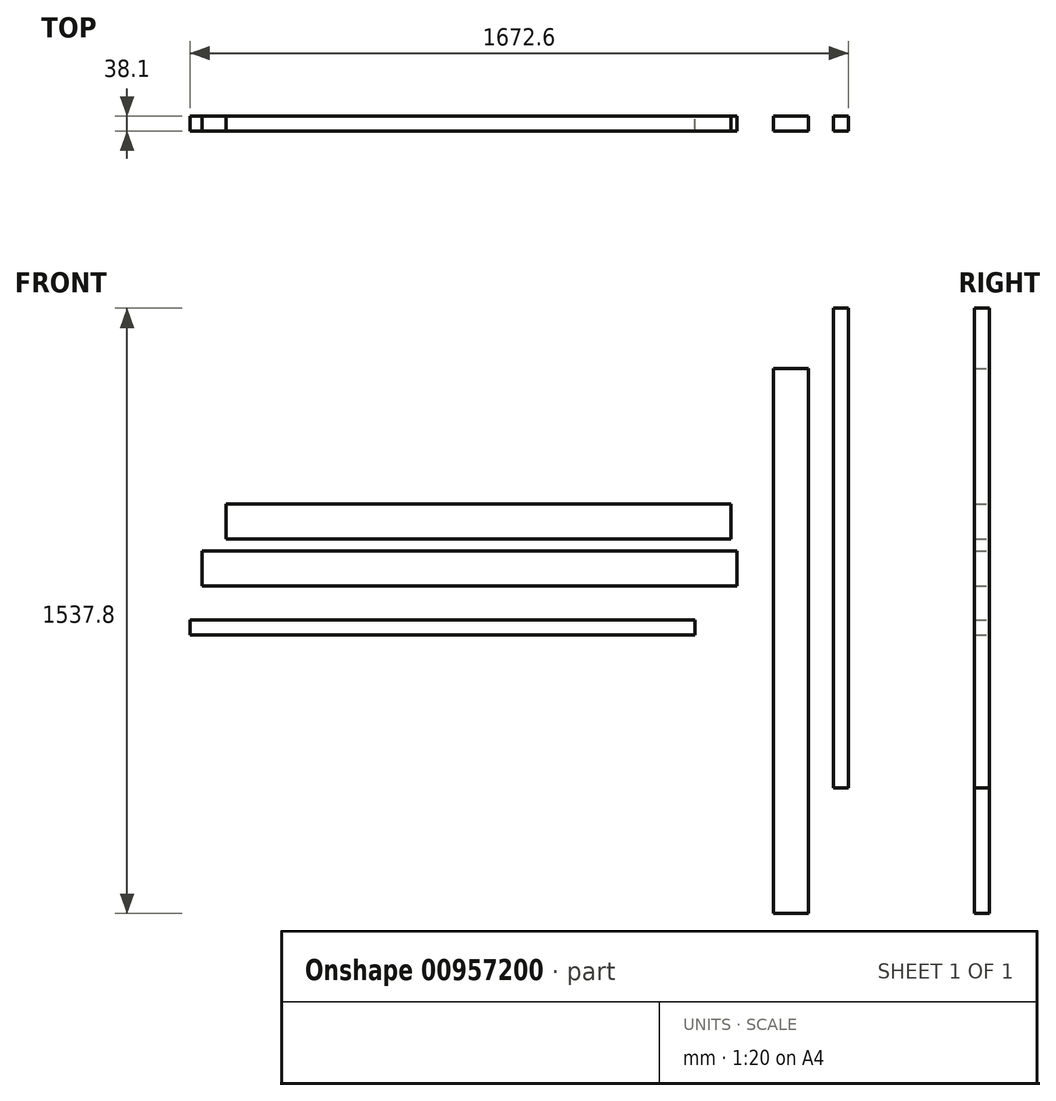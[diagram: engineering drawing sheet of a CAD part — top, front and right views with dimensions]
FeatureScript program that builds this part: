
annotation { "Feature Type Name" : "Feature", "Feature Type Description" : "" }
export const myFeature = defineFeature(function(context is Context, id is Id, definition is map)
    precondition{}
    {
        {
            var Q0;
            Q0=qCreatedBy(makeId("Front.planeOp"),FACE);
            var sketch = newSketch(context, id + "F0", { "sketchPlane" : qUnion([Q0])});
            skLineSegment(sketch, "E0.bottom", {"start": v(471.1, 163.2) * mm, "end": v(-811.6, 163.2) * mm});
            skLineSegment(sketch, "E0.top", {"start": v(471.1, 74.3) * mm, "end": v(-811.6, 74.3) * mm});
            skLineSegment(sketch, "E0.left", {"start": v(471.1, 163.2) * mm, "end": v(471.1, 74.3) * mm});
            skLineSegment(sketch, "E0.right", {"start": v(-811.6, 163.2) * mm, "end": v(-811.6, 74.3) * mm});
            skPoint(sketch, "E0.middle", {"position": v(-170.25, 118.74) * mm});
            skSolve(sketch);
        }
        {
            var Q0;
            Q0=qCreatedBy(makeId("Front.planeOp"),FACE);
            var sketch = newSketch(context, id + "F1", { "sketchPlane" : qUnion([Q0])});
            skLineSegment(sketch, "E1.bottom", {"start": v(487.25, -44.45) * mm, "end": v(-871.65, -44.45) * mm});
            skLineSegment(sketch, "E1.top", {"start": v(487.25, 44.45) * mm, "end": v(-871.65, 44.45) * mm});
            skLineSegment(sketch, "E1.left", {"start": v(487.25, -44.45) * mm, "end": v(487.25, 44.45) * mm});
            skLineSegment(sketch, "E1.right", {"start": v(-871.65, -44.45) * mm, "end": v(-871.65, 44.45) * mm});
            skPoint(sketch, "E1.middle", {"position": v(-192.2, 0) * mm});
            skSolve(sketch);
        }
        {
            var Q0;
            Q0=qCreatedBy(makeId("Front.planeOp"),FACE);
            var sketch = newSketch(context, id + "F2", { "sketchPlane" : qUnion([Q0])});
            skLineSegment(sketch, "E2.bottom", {"start": v(668.46, 507.39) * mm, "end": v(579.56, 507.39) * mm});
            skLineSegment(sketch, "E2.top", {"start": v(668.46, -876.91) * mm, "end": v(579.56, -876.91) * mm});
            skLineSegment(sketch, "E2.left", {"start": v(668.46, 507.39) * mm, "end": v(668.46, -876.91) * mm});
            skLineSegment(sketch, "E2.right", {"start": v(579.56, 507.39) * mm, "end": v(579.56, -876.91) * mm});
            skPoint(sketch, "E2.middle", {"position": v(624.01, -184.76) * mm});
            skSolve(sketch);
        }
        {
            var Q0;
            Q0=qSketchRegion(id+"F0",true);
            extrude(context, id + "F3", {"entities" : qUnion([Q0]), "depth" : 38.1 * mm, "offsetDistance" : 25.4 * mm});
        }
        {
            var Q0;
            Q0=makeQuery(id+"F1.imprint","IMPRINT",FACE,{"disambiguationData":[TD([[makeQuery(id+"F1.imprint","IMPRINT",EDGE,{"derivedFrom":sQuery(id+"F1.wireOp",EDGE,"E1.bottom")}),-1.0]])]});
            extrude(context, id + "F4", {"entities" : qUnion([Q0]), "depth" : 38.1 * mm, "offsetDistance" : 25.4 * mm});
        }
        {
            var Q0;
            Q0=makeQuery(id+"F2.imprint","IMPRINT",FACE,{"disambiguationData":[TD([[makeQuery(id+"F2.imprint","IMPRINT",EDGE,{"derivedFrom":sQuery(id+"F2.wireOp",EDGE,"E2.bottom")}),1.0]])]});
            extrude(context, id + "F5", {"entities" : qUnion([Q0]), "depth" : 38.1 * mm, "offsetDistance" : 25.4 * mm});
        }
        {
            var Q0;
            Q0=qCreatedBy(makeId("Front.planeOp"),FACE);
            var sketch = newSketch(context, id + "F6", { "sketchPlane" : qUnion([Q0])});
            skLineSegment(sketch, "E3.bottom", {"start": v(380.07, -168.87) * mm, "end": v(-902.63, -168.87) * mm});
            skLineSegment(sketch, "E3.top", {"start": v(380.07, -130.77) * mm, "end": v(-902.63, -130.77) * mm});
            skLineSegment(sketch, "E3.left", {"start": v(380.07, -168.87) * mm, "end": v(380.07, -130.77) * mm});
            skLineSegment(sketch, "E3.right", {"start": v(-902.63, -168.87) * mm, "end": v(-902.63, -130.77) * mm});
            skPoint(sketch, "E3.middle", {"position": v(-261.28, -149.82) * mm});
            skSolve(sketch);
        }
        {
            var Q0;
            Q0=qCreatedBy(makeId("Front.planeOp"),FACE);
            var sketch = newSketch(context, id + "F7", { "sketchPlane" : qUnion([Q0])});
            skLineSegment(sketch, "E4.bottom", {"start": v(769.97, 660.9) * mm, "end": v(731.87, 660.9) * mm});
            skLineSegment(sketch, "E4.top", {"start": v(769.97, -558.3) * mm, "end": v(731.87, -558.3) * mm});
            skLineSegment(sketch, "E4.left", {"start": v(769.97, 660.9) * mm, "end": v(769.97, -558.3) * mm});
            skLineSegment(sketch, "E4.right", {"start": v(731.87, 660.9) * mm, "end": v(731.87, -558.3) * mm});
            skPoint(sketch, "E4.middle", {"position": v(750.92, 51.3) * mm});
            skSolve(sketch);
        }
        {
            var Q0;
            Q0=makeQuery(id+"F6.imprint","IMPRINT",FACE,{"disambiguationData":[TD([[makeQuery(id+"F6.imprint","IMPRINT",EDGE,{"derivedFrom":sQuery(id+"F6.wireOp",EDGE,"E3.bottom")}),-1.0]])]});
            extrude(context, id + "F8", {"entities" : qUnion([Q0]), "depth" : 38.1 * mm, "offsetDistance" : 25.4 * mm});
        }
        {
            var Q0;
            Q0=makeQuery(id+"F7.imprint","IMPRINT",FACE,{"disambiguationData":[TD([[makeQuery(id+"F7.imprint","IMPRINT",EDGE,{"derivedFrom":sQuery(id+"F7.wireOp",EDGE,"E4.bottom")}),1.0]])]});
            extrude(context, id + "F9", {"entities" : qUnion([Q0]), "depth" : 38.1 * mm, "offsetDistance" : 25.4 * mm});
        }
    });
